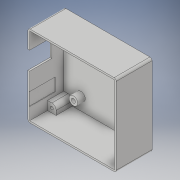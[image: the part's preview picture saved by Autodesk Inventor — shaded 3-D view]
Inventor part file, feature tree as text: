
AUTODESK INVENTOR PART (.ipt)
format: ipt  version: 2019 (Build 230136000, 136)  size: 449,536 bytes
history: native  units: mm
features: other x11, extrude x6, hole x2, loft x1, fillet x1
ambient origin geometry x8: Origin, YZ Plane, XZ Plane, XY Plane, X Axis, Y Axis, Z Axis, Center Point
bodies: Solid1 (feature_tree)
feature tree (21):
  extrude  "Extrusion1"  Depth=78.5mm
  other  "Uchyt_arduino"
  other  "Spojeni_srouby"
  extrude  "Extrusion2"  Depth=72.0mm
  extrude  "Extrusion5"  Depth=1.2mm TaperAngle=0.0deg
  hole  "Hole6"  [1 undecoded]
  extrude  "Extrusion6"  Depth=8.0mm
  extrude  "Extrusion7"  Depth=7.0mm TaperAngle=0.0deg
  hole  "Hole7"  [1 undecoded]
  other  "napajeni_znacka1"
  other  "napajeni_znacka2_rovina"
  loft  "Loft4"
  extrude  "Extrusion8"  Depth=15.45mm
  fillet  "Fillet1"  Radius=1.6mm
  other  "Zakladna"
  other  "diry_srouby"
  other  "steny"
  other  "stena_RJ45"
  other  "arduino_uchyt_zavitovaVlozka"
  other  "napajeni_znacka2"
  other  "vyrez_nepouzity_jack"
note: 2 required parameter values undecoded (feature->parameter linkage not recoverable at this tier; creation-order binding heuristic only, values carry confidence <= 0.55)
